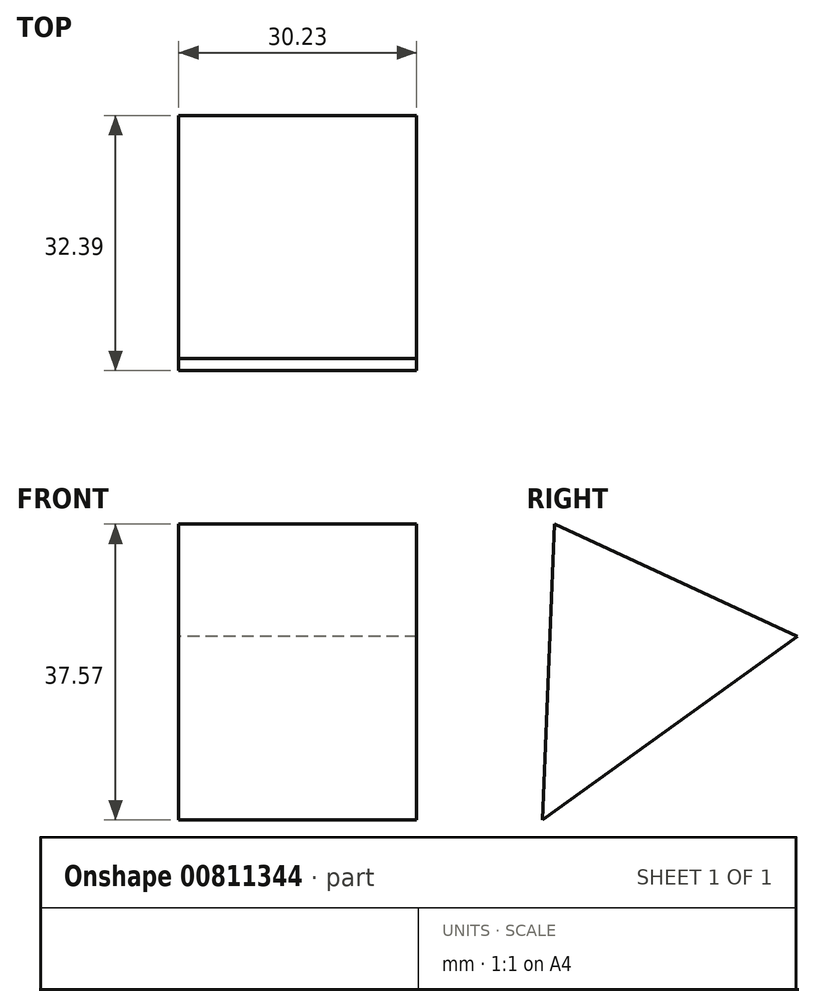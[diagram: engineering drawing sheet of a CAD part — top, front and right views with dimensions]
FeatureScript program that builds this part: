
annotation { "Feature Type Name" : "Feature", "Feature Type Description" : "" }
export const myFeature = defineFeature(function(context is Context, id is Id, definition is map)
    precondition{}
    {
        {
            var Q0;
            Q0=qCreatedBy(makeId("Right.planeOp"),FACE);
            var sketch = newSketch(context, id + "F0", { "sketchPlane" : qUnion([Q0])});
            skLineSegment(sketch, "E0", {"start": v(-36.17, -48.37) * mm, "end": v(-34.66, -10.8) * mm});
            skLineSegment(sketch, "E1", {"start": v(-34.66, -10.8) * mm, "end": v(-3.78, -25.05) * mm});
            skLineSegment(sketch, "E2", {"start": v(-3.78, -25.05) * mm, "end": v(-36.17, -48.37) * mm});
            skSolve(sketch);
        }
        {
            var Q0;
            Q0=makeQuery(id+"F0.imprint","IMPRINT",FACE,{"disambiguationData":[TD([[makeQuery(id+"F0.imprint","IMPRINT",EDGE,{"derivedFrom":sQuery(id+"F0.wireOp",EDGE,"E0")}),-1.0]])]});
            extrude(context, id + "F1", {"entities" : qUnion([Q0]), "depth" : 30.23 * mm, "offsetDistance" : 25.4 * mm});
        }
    });
